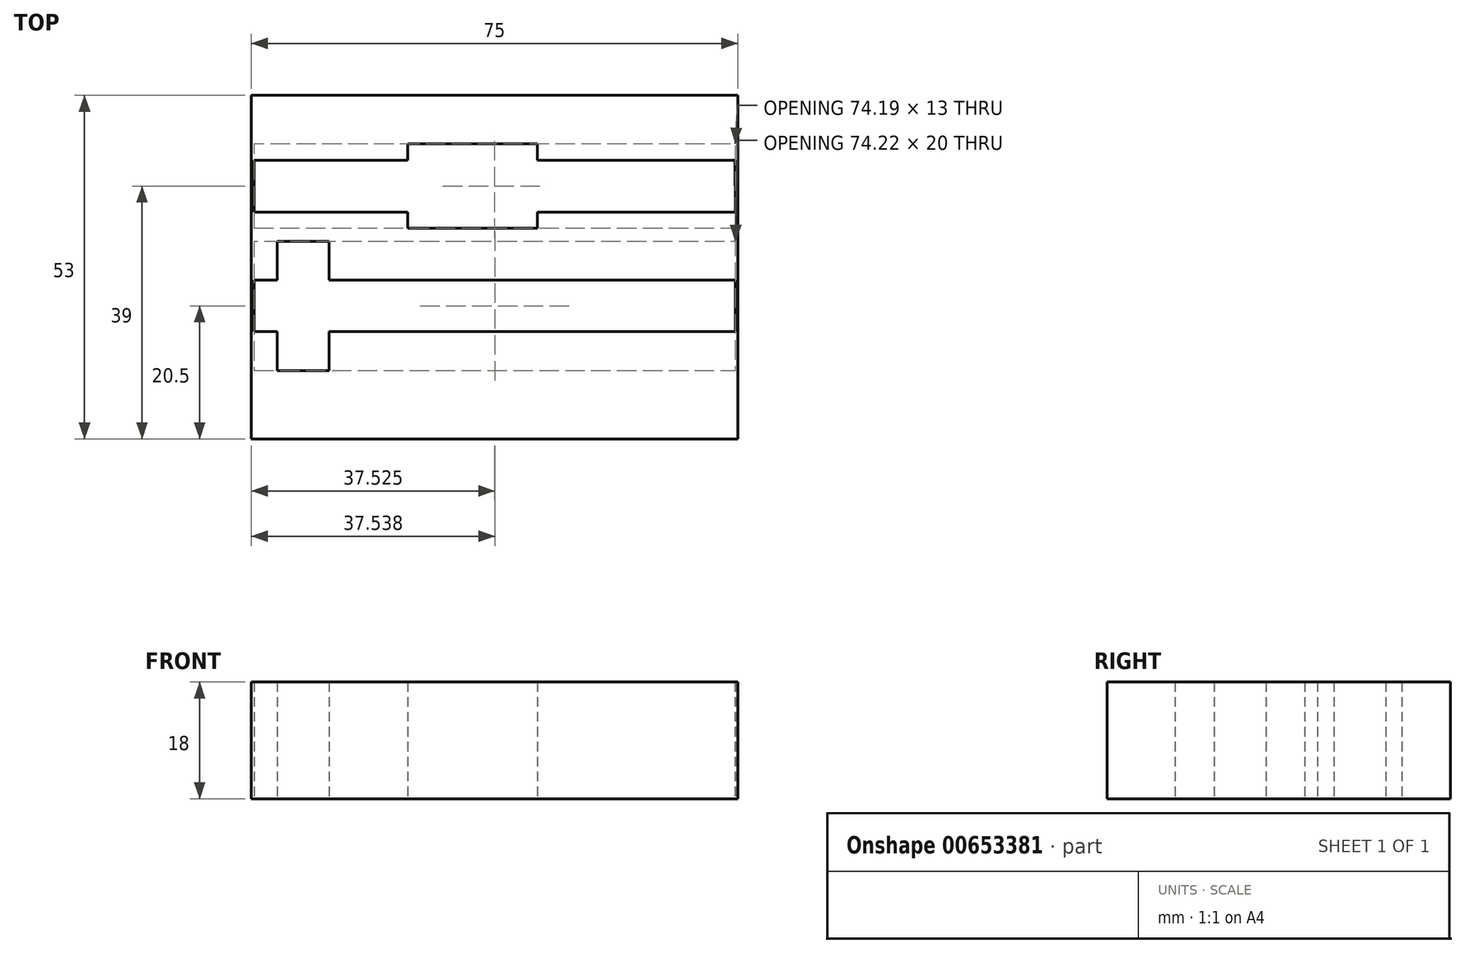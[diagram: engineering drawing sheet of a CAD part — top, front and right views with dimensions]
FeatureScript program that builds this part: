
annotation { "Feature Type Name" : "Feature", "Feature Type Description" : "" }
export const myFeature = defineFeature(function(context is Context, id is Id, definition is map)
    precondition{}
    {
        {
            var Q0;
            Q0=qCreatedBy(makeId("Top.planeOp"),FACE);
            var sketch = newSketch(context, id + "F0", { "sketchPlane" : qUnion([Q0])});
            skLineSegment(sketch, "E0.bottom", {"start": v(37.5, -30.5) * mm, "end": v(-37.5, -30.5) * mm});
            skLineSegment(sketch, "E0.top", {"start": v(37.5, 22.5) * mm, "end": v(-37.5, 22.5) * mm});
            skPoint(sketch, "E0.middle", {"position": v(0, 0) * mm});
            skLineSegment(sketch, "E1", {"start": v(-25.5, -20) * mm, "end": v(-25.5, -13.97) * mm});
            skLineSegment(sketch, "E2", {"start": v(-25.5, 0) * mm, "end": v(-33.5, 0) * mm});
            skLineSegment(sketch, "E3", {"start": v(-25.5, -20) * mm, "end": v(-33.5, -20) * mm});
            skPoint(sketch, "E4.start.orphan", {"position": v(-37.5, 0) * mm});
            skLineSegment(sketch, "E5", {"start": v(-33.5, 0) * mm, "end": v(-33.5, -5.97) * mm});
            skPoint(sketch, "E6", {"position": v(-37.5, -9.97) * mm});
            skPoint(sketch, "E7.start.orphan", {"position": v(-29.5, 0) * mm});
            skLineSegment(sketch, "E8", {"start": v(-37.07, -5.97) * mm, "end": v(-33.5, -5.97) * mm});
            skLineSegment(sketch, "E9", {"start": v(-37.07, -13.97) * mm, "end": v(-33.5, -13.97) * mm});
            skLineSegment(sketch, "E10", {"start": v(-25.5, -5.97) * mm, "end": v(37.14, -5.97) * mm});
            skLineSegment(sketch, "E11", {"start": v(-25.5, -13.97) * mm, "end": v(37.15, -13.97) * mm});
            skLineSegment(sketch, "E12.trimOffspring", {"start": v(-33.5, -13.97) * mm, "end": v(-33.5, -20) * mm});
            skLineSegment(sketch, "E13.trimOffspring", {"start": v(-25.5, -5.97) * mm, "end": v(-25.5, 0) * mm});
            skLineSegment(sketch, "E14", {"start": v(-13.38, 15) * mm, "end": v(-13.38, 12.5) * mm});
            skLineSegment(sketch, "E15", {"start": v(-13.38, 2) * mm, "end": v(6.62, 2) * mm});
            skLineSegment(sketch, "E16", {"start": v(6.62, 2) * mm, "end": v(6.62, 4.5) * mm});
            skLineSegment(sketch, "E17", {"start": v(6.62, 15) * mm, "end": v(-13.38, 15) * mm});
            skLineSegment(sketch, "E18", {"start": v(-13.38, 12.5) * mm, "end": v(-37.07, 12.5) * mm});
            skLineSegment(sketch, "E19", {"start": v(-13.38, 4.5) * mm, "end": v(-37.07, 4.5) * mm});
            skLineSegment(sketch, "E20", {"start": v(6.62, 12.5) * mm, "end": v(37.1, 12.5) * mm});
            skLineSegment(sketch, "E21", {"start": v(6.62, 4.5) * mm, "end": v(37.12, 4.5) * mm});
            skLineSegment(sketch, "E22.trimOffspring", {"start": v(-13.38, 4.5) * mm, "end": v(-13.38, 2) * mm});
            skLineSegment(sketch, "E23.trimOffspring", {"start": v(6.62, 12.5) * mm, "end": v(6.62, 15) * mm});
            skLineSegment(sketch, "E24", {"start": v(37.5, 22.5) * mm, "end": v(37.5, -22.5) * mm});
            skLineSegment(sketch, "E25", {"start": v(-37.5, 22.5) * mm, "end": v(-37.5, -22.5) * mm});
            skLineSegment(sketch, "E26", {"start": v(-37.07, 12.5) * mm, "end": v(-37.07, 4.5) * mm});
            skLineSegment(sketch, "E27", {"start": v(-37.07, -5.97) * mm, "end": v(-37.07, -13.97) * mm});
            skPoint(sketch, "E27.endSnap0", {"position": v(-35.5, -13.97) * mm});
            skPoint(sketch, "E28.orphan", {"position": v(-37.5, -13.97) * mm});
            skLineSegment(sketch, "E29", {"start": v(37.1, 12.5) * mm, "end": v(37.12, 4.5) * mm});
            skLineSegment(sketch, "E30.trimOffspring", {"start": v(37.14, -5.97) * mm, "end": v(37.15, -13.97) * mm});
            skLineSegment(sketch, "E31", {"start": v(-37.5, -30.5) * mm, "end": v(-37.5, -22.5) * mm});
            skLineSegment(sketch, "E32", {"start": v(37.5, -30.5) * mm, "end": v(37.5, -22.5) * mm});
            skSolve(sketch);
        }
        {
            var Q0;
            Q0 = qSketchRegion(id + "F0", true);
            extrude(context, id + "F1", {"entities" : qUnion([Q0]), "depth" : 18 * mm, "offsetDistance" : 25 * mm});
        }
    });
